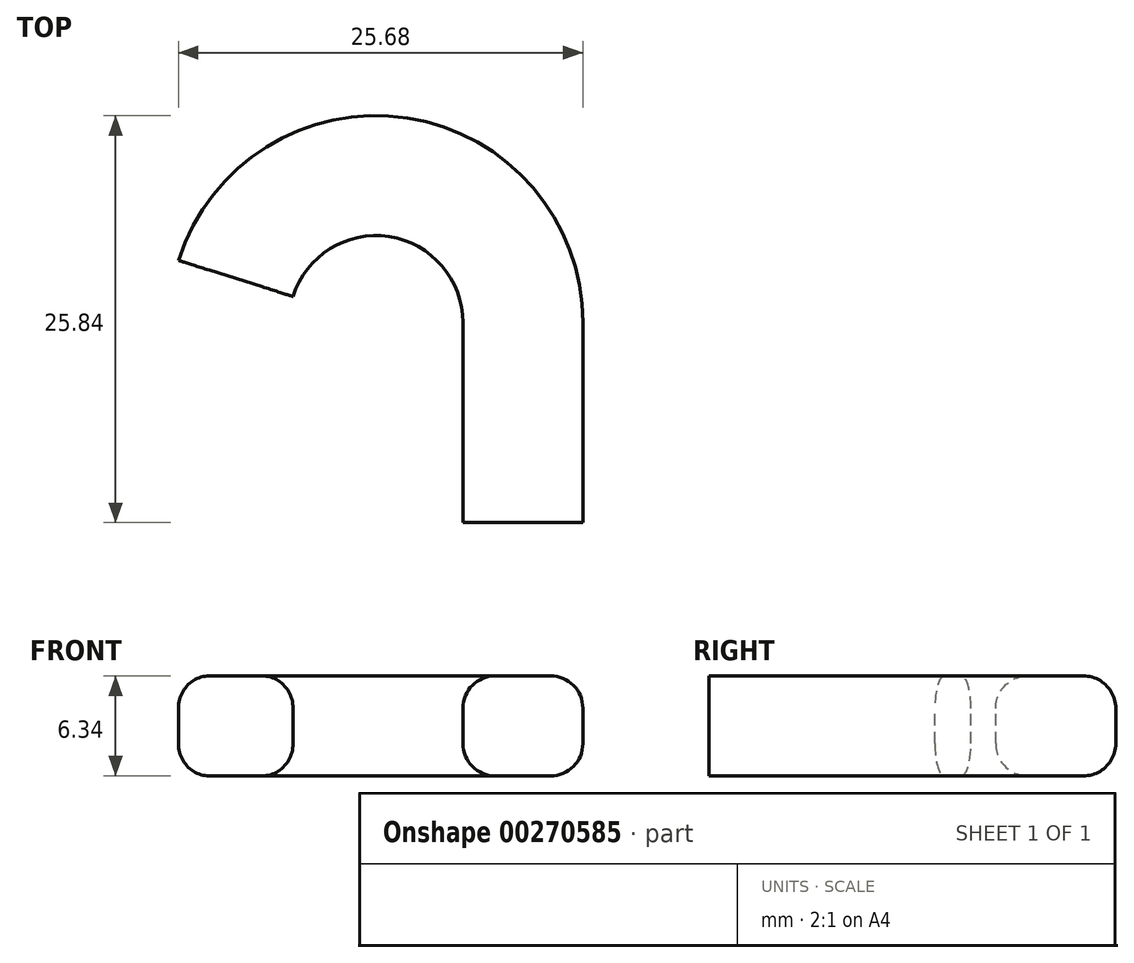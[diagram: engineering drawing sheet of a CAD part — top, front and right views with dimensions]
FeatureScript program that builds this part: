
annotation { "Feature Type Name" : "Feature", "Feature Type Description" : "" }
export const myFeature = defineFeature(function(context is Context, id is Id, definition is map)
    precondition{}
    {
        {
            var Q0;
            Q0=qCreatedBy(makeId("Front.planeOp"),FACE);
            var sketch = newSketch(context, id + "F0", { "sketchPlane" : qUnion([Q0])});
            skLineSegment(sketch, "E0.bottom", {"start": v(1.76, -3.18) * mm, "end": v(-1.76, -3.18) * mm});
            skLineSegment(sketch, "E0.top", {"start": v(1.76, 3.18) * mm, "end": v(-1.76, 3.18) * mm});
            skLineSegment(sketch, "E0.left", {"start": v(3.81, -1.12) * mm, "end": v(3.81, 1.12) * mm});
            skLineSegment(sketch, "E0.right", {"start": v(-3.81, -1.12) * mm, "end": v(-3.81, 1.12) * mm});
            skPoint(sketch, "E0.middle", {"position": v(0, 0) * mm});
            skPoint(sketch, "E1.visualSharp", {"position": v(-3.81, 3.17) * mm});
            skArc(sketch, "E1.filletArc", {"start": v(-1.76, 3.18) * mm, "mid": v(-3.2, 2.57) * mm, "end": v(-3.81, 1.12) * mm});
            skPoint(sketch, "E2.visualSharp", {"position": v(-3.81, -3.18) * mm});
            skArc(sketch, "E2.filletArc", {"start": v(-3.81, -1.12) * mm, "mid": v(-3.2, -2.57) * mm, "end": v(-1.76, -3.18) * mm});
            skPoint(sketch, "E3.visualSharp", {"position": v(3.81, -3.17) * mm});
            skArc(sketch, "E3.filletArc", {"start": v(1.76, -3.18) * mm, "mid": v(3.2, -2.57) * mm, "end": v(3.81, -1.12) * mm});
            skPoint(sketch, "E4.visualSharp", {"position": v(3.81, 3.18) * mm});
            skArc(sketch, "E4.filletArc", {"start": v(3.81, 1.12) * mm, "mid": v(3.2, 2.57) * mm, "end": v(1.76, 3.18) * mm});
            skSolve(sketch);
        }
        {
            var Q0;
            Q0=qCreatedBy(makeId("Top.planeOp"),FACE);
            var sketch = newSketch(context, id + "F1", { "sketchPlane" : qUnion([Q0])});
            skLineSegment(sketch, "E5", {"start": v(0, 0) * mm, "end": v(0, 12.7) * mm});
            skArc(sketch, "E6", {"start": v(0, 12.7) * mm, "mid": v(-7.92, 21.92) * mm, "end": v(-18.24, 15.5) * mm});
            skSolve(sketch);
        }
        {
            var Q0;
            Q0=makeQuery(id+"F0.imprint","IMPRINT",FACE,{"disambiguationData":[TD([[makeQuery(id+"F0.imprint","IMPRINT",EDGE,{"derivedFrom":sQuery(id+"F0.wireOp",EDGE,"E0.bottom")}),-1.0]])]});
            var Q1;
            Q1=sQuery(id+"F1.wireOp",EDGE,"E5");
            var Q2;
            Q2=sQuery(id+"F1.wireOp",EDGE,"E6");
            sweep(context, id + "F2", {"profiles" : qUnion([Q0]), "path" : qUnion([Q1, Q2])});
        }
    });
